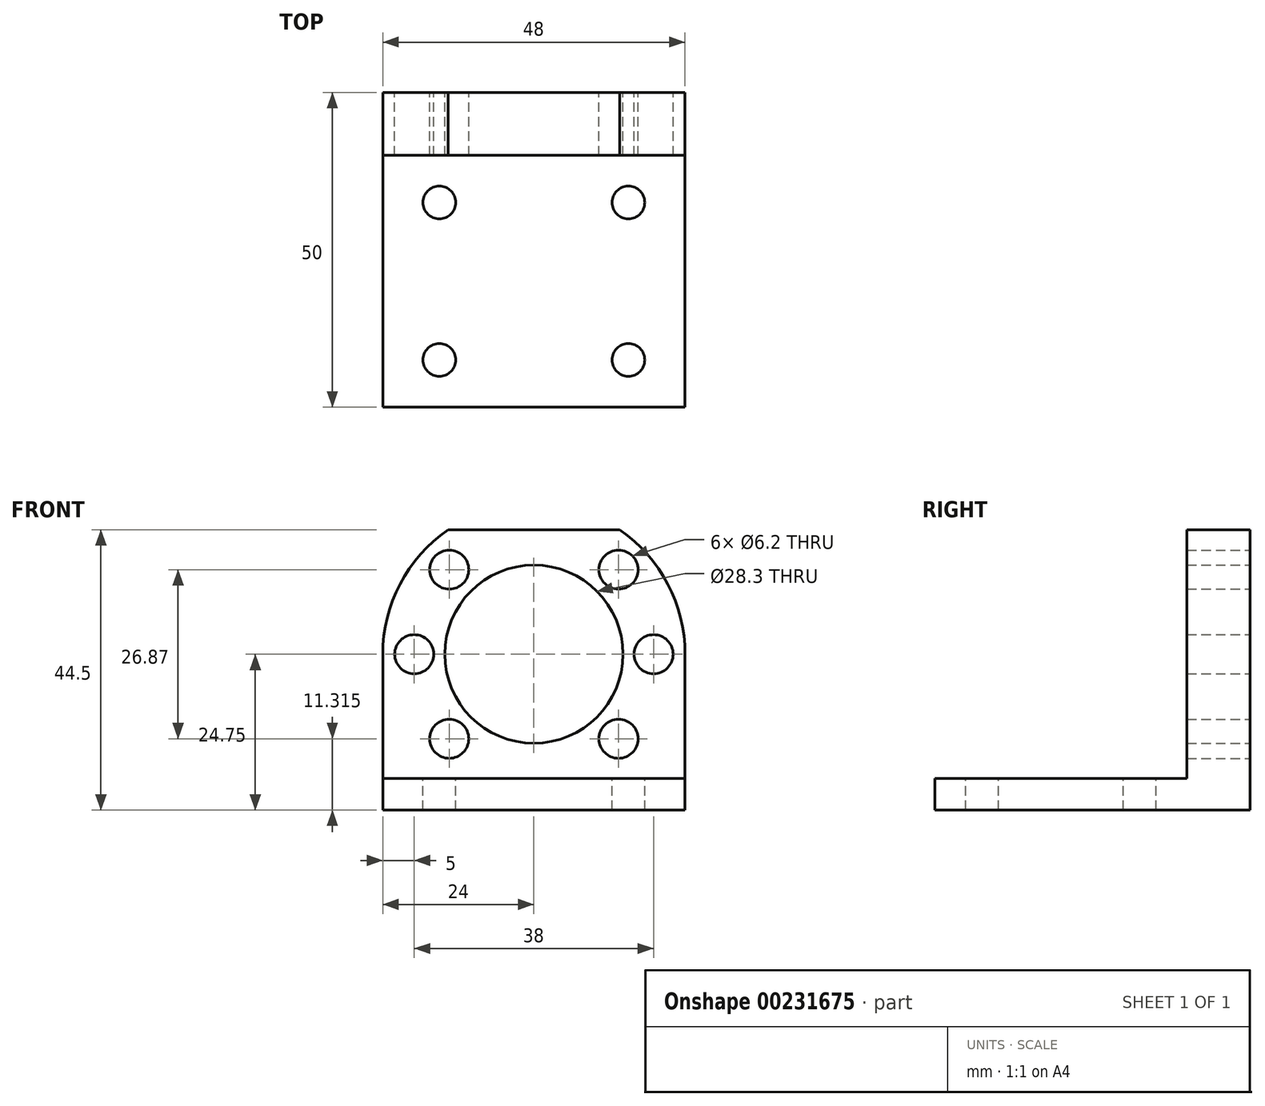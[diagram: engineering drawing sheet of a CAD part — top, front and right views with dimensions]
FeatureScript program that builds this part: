
annotation { "Feature Type Name" : "Feature", "Feature Type Description" : "" }
export const myFeature = defineFeature(function(context is Context, id is Id, definition is map)
    precondition{}
    {
        {
            var Q0;
            Q0=qCreatedBy(makeId("Front.planeOp"),FACE);
            var sketch = newSketch(context, id + "F0", { "sketchPlane" : qUnion([Q0])});
            skCircle(sketch, "E0", {"center": v(0, 0) * mm, "radius": 14.15 * mm});
            skArc(sketch, "E1", {"start": v(-13.64, 19.75) * mm, "mid": v(-21.25, 11.15) * mm, "end": v(-24, 0) * mm});
            skLineSegment(sketch, "E2", {"start": v(-13.64, 19.75) * mm, "end": v(13.64, 19.75) * mm});
            skLineSegment(sketch, "E3", {"start": v(24, 0) * mm, "end": v(-24, 0) * mm, "construction": true});
            skCircle(sketch, "E4", {"center": v(0, 0) * mm, "radius": 19 * mm, "construction": true});
            skCircle(sketch, "E5", {"center": v(-13.44, 13.44) * mm, "radius": 3.1 * mm});
            skCircle(sketch, "E6", {"center": v(-19, 0) * mm, "radius": 3.1 * mm});
            skCircle(sketch, "E7", {"center": v(-13.44, -13.44) * mm, "radius": 3.1 * mm});
            skCircle(sketch, "E8", {"center": v(13.44, -13.44) * mm, "radius": 3.1 * mm});
            skCircle(sketch, "E9", {"center": v(19, 0) * mm, "radius": 3.1 * mm});
            skCircle(sketch, "E10", {"center": v(13.44, 13.44) * mm, "radius": 3.1 * mm});
            skLineSegment(sketch, "E11", {"start": v(0, 24) * mm, "end": v(0, -24) * mm, "construction": true});
            skLineSegment(sketch, "E12", {"start": v(-16.97, 16.97) * mm, "end": v(16.97, -16.97) * mm, "construction": true});
            skLineSegment(sketch, "E13", {"start": v(-24, 0) * mm, "end": v(-24, -24.75) * mm});
            skLineSegment(sketch, "E14", {"start": v(24, 0) * mm, "end": v(24, -24.75) * mm});
            skLineSegment(sketch, "E15", {"start": v(24, -24.75) * mm, "end": v(-24, -24.75) * mm});
            skArc(sketch, "E16.trimOffspring", {"start": v(24, 0) * mm, "mid": v(21.25, 11.15) * mm, "end": v(13.64, 19.75) * mm});
            skCircle(sketch, "E17", {"center": v(0, 0) * mm, "radius": 24 * mm, "construction": true});
            skSolve(sketch);
        }
        {
            var Q0;
            Q0 = qSketchRegion(id + "F0", true);
            extrude(context, id + "F1", {"entities" : qUnion([Q0]), "depth" : 10 * mm});
        }
        {
            var Q0;
            Q0=makeQuery(id+"F1.opExtrude","CAP_FACE",FACE,{"disambiguationData":[OSD([sQuery(id+"F0.wireOp",EDGE,"E0"),sQuery(id+"F0.wireOp",EDGE,"E1"),sQuery(id+"F0.wireOp",EDGE,"E2"),sQuery(id+"F0.wireOp",EDGE,"E5"),sQuery(id+"F0.wireOp",EDGE,"E6"),sQuery(id+"F0.wireOp",EDGE,"E7"),sQuery(id+"F0.wireOp",EDGE,"E8"),sQuery(id+"F0.wireOp",EDGE,"E9"),sQuery(id+"F0.wireOp",EDGE,"E10"),sQuery(id+"F0.wireOp",EDGE,"E13"),sQuery(id+"F0.wireOp",EDGE,"E14"),sQuery(id+"F0.wireOp",EDGE,"E15"),sQuery(id+"F0.wireOp",EDGE,"E16.trimOffspring")])],"isStart":false});
            var sketch = newSketch(context, id + "F2", { "sketchPlane" : qUnion([Q0])});
            skLineSegment(sketch, "E18.bottom", {"start": v(-24, -24.75) * mm, "end": v(24, -24.75) * mm});
            skLineSegment(sketch, "E18.top", {"start": v(-24, -19.75) * mm, "end": v(24, -19.75) * mm});
            skLineSegment(sketch, "E18.left", {"start": v(-24, -24.75) * mm, "end": v(-24, -19.75) * mm});
            skLineSegment(sketch, "E18.right", {"start": v(24, -24.75) * mm, "end": v(24, -19.75) * mm});
            skSolve(sketch);
        }
        {
            var Q0;
            Q0 = qSketchRegion(id + "F2", true);
            extrude(context, id + "F3", {"entities" : qUnion([Q0]), "operationType" : NewBodyOperationType.ADD, "depth" : 40 * mm});
        }
        {
            var Q0;
            Q0=makeQuery(id+"F3.opExtrude","SWEPT_FACE",FACE,{"disambiguationData":[OSD([sQuery(id+"F2.wireOp",EDGE,"E18.top")])]});
            var sketch = newSketch(context, id + "F4", { "sketchPlane" : qUnion([Q0])});
            skLineSegment(sketch, "E19", {"start": v(-24, -10) * mm, "end": v(24, -50) * mm, "construction": true});
            skLineSegment(sketch, "E20", {"start": v(24, -10) * mm, "end": v(-24, -50) * mm, "construction": true});
            skCircle(sketch, "E21", {"center": v(-15, -17.5) * mm, "radius": 2.6 * mm});
            skCircle(sketch, "E22", {"center": v(-15, -42.5) * mm, "radius": 2.6 * mm});
            skCircle(sketch, "E23", {"center": v(15, -42.5) * mm, "radius": 2.6 * mm});
            skCircle(sketch, "E24", {"center": v(15, -17.5) * mm, "radius": 2.6 * mm});
            skLineSegment(sketch, "E25", {"start": v(0, -10) * mm, "end": v(0, -50) * mm, "construction": true});
            skLineSegment(sketch, "E26", {"start": v(24, -30) * mm, "end": v(-24, -30) * mm, "construction": true});
            skSolve(sketch);
        }
        {
            var Q0;
            Q0 = qSketchRegion(id + "F4", true);
            extrude(context, id + "F5", {"entities" : qUnion([Q0]), "operationType" : NewBodyOperationType.REMOVE, "endBound" : BoundingType.UP_TO_NEXT, "oppositeDirection" : true, "depth" : 25 * mm});
        }
    });
